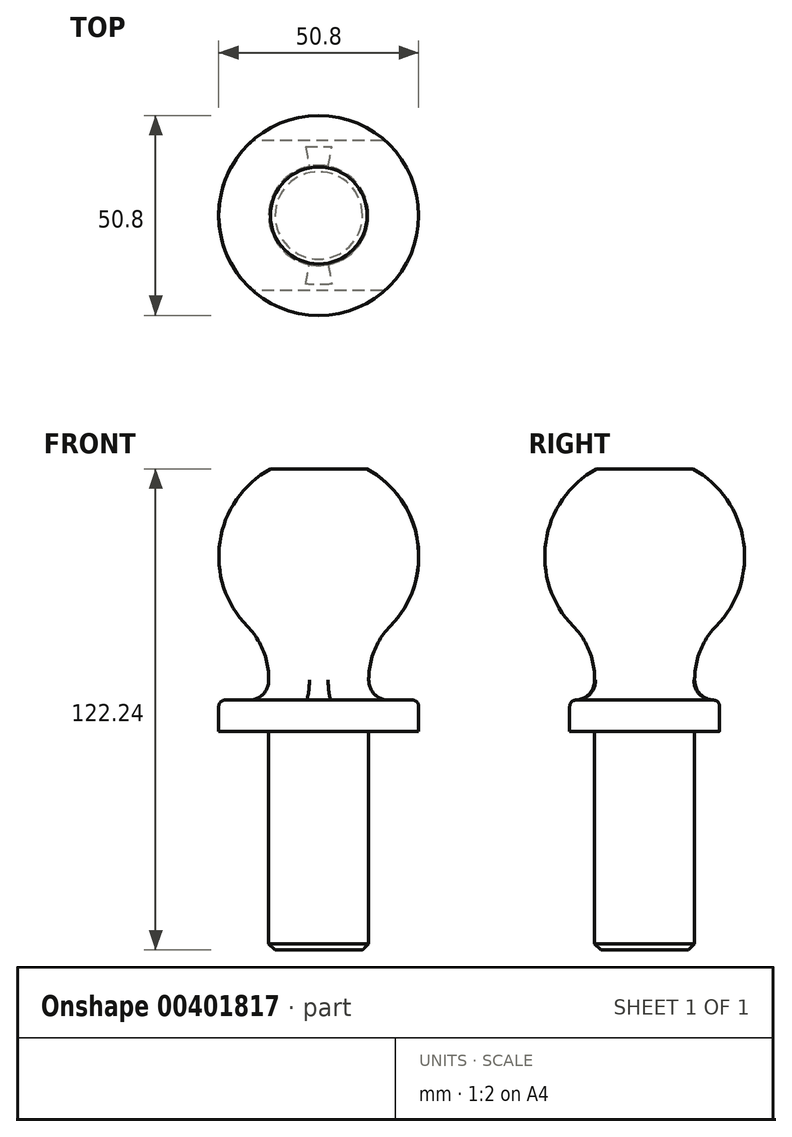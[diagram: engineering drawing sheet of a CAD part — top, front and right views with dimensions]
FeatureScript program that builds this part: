
annotation { "Feature Type Name" : "Feature", "Feature Type Description" : "" }
export const myFeature = defineFeature(function(context is Context, id is Id, definition is map)
    precondition{}
    {
        {
            var Q0;
            Q0=qCreatedBy(makeId("Front.planeOp"),FACE);
            var sketch = newSketch(context, id + "F0", { "sketchPlane" : qUnion([Q0])});
            skLineSegment(sketch, "E0.bottom", {"start": v(-12.7, 0) * mm, "end": v(-25.4, 0) * mm});
            skLineSegment(sketch, "E0.top", {"start": v(-12.7, 7.94) * mm, "end": v(-25.4, 7.94) * mm});
            skLineSegment(sketch, "E0.left", {"start": v(0, 0) * mm, "end": v(0, 7.94) * mm});
            skLineSegment(sketch, "E0.right", {"start": v(-25.4, 0) * mm, "end": v(-25.4, 7.94) * mm});
            skPoint(sketch, "E1", {"position": v(-12.7, 22.45) * mm});
            skPoint(sketch, "E2", {"position": v(0, 19.05) * mm});
            skLineSegment(sketch, "E3", {"start": v(-12.7, 22.45) * mm, "end": v(-12.7, 7.94) * mm});
            skPoint(sketch, "E4", {"position": v(-12.7, 7.94) * mm});
            skLineSegment(sketch, "E5", {"start": v(0, 66.68) * mm, "end": v(0, 19.05) * mm});
            skLineSegment(sketch, "E6", {"start": v(0, 19.05) * mm, "end": v(0, 7.94) * mm});
            skArc(sketch, "E7", {"start": v(-12.3, 66.68) * mm, "mid": v(-25.4, 44.68) * mm, "end": v(-12.7, 22.45) * mm});
            skLineSegment(sketch, "E8", {"start": v(0, 66.68) * mm, "end": v(-12.3, 66.68) * mm});
            skLineSegment(sketch, "E9.top", {"start": v(0, -55.56) * mm, "end": v(-12.7, -55.56) * mm});
            skLineSegment(sketch, "E9.left", {"start": v(0, 0) * mm, "end": v(0, -55.56) * mm});
            skLineSegment(sketch, "E9.right", {"start": v(-12.7, 0) * mm, "end": v(-12.7, -55.56) * mm});
            skSolve(sketch);
        }
        {
            var Q0;
            Q0 = qSketchRegion(id + "F0", true);
            var Q1;
            Q1=sQuery(id+"F0.wireOp",EDGE,"E9.left");
            revolve(context, id + "F1", {"entities" : qUnion([Q0]), "axis" : qUnion([Q1]), "revolveType" : RevolveType.FULL});
        }
        {
            var Q0;
            Q0=qCreatedBy(makeId("Right.planeOp"),FACE);
            var sketch = newSketch(context, id + "F2", { "sketchPlane" : qUnion([Q0])});
            skLineSegment(sketch, "E10.bottom", {"start": v(-49.59, -5.38) * mm, "end": v(-19.05, -5.38) * mm});
            skLineSegment(sketch, "E10.top", {"start": v(-49.59, 14.79) * mm, "end": v(-19.05, 14.79) * mm});
            skLineSegment(sketch, "E10.left", {"start": v(-49.59, -5.38) * mm, "end": v(-49.59, 14.79) * mm});
            skLineSegment(sketch, "E10.right", {"start": v(-19.05, -5.38) * mm, "end": v(-19.05, 14.79) * mm});
            skLineSegment(sketch, "E11.bottom", {"start": v(19.05, -5.38) * mm, "end": v(49.59, -5.38) * mm});
            skLineSegment(sketch, "E11.top", {"start": v(19.05, 14.79) * mm, "end": v(49.59, 14.79) * mm});
            skLineSegment(sketch, "E11.left", {"start": v(19.05, -5.38) * mm, "end": v(19.05, 14.79) * mm});
            skLineSegment(sketch, "E11.right", {"start": v(49.59, -5.38) * mm, "end": v(49.59, 14.79) * mm});
            skSolve(sketch);
        }
        {
            var Q0;
            Q0=makeQuery(id+"F2.imprint","IMPRINT",FACE,{"disambiguationData":[TD([[makeQuery(id+"F2.imprint","IMPRINT",EDGE,{"derivedFrom":sQuery(id+"F2.wireOp",EDGE,"E10.bottom")}),1.0]])]});
            var Q1;
            Q1=makeQuery(id+"F2.imprint","IMPRINT",FACE,{"disambiguationData":[TD([[makeQuery(id+"F2.imprint","IMPRINT",EDGE,{"derivedFrom":sQuery(id+"F2.wireOp",EDGE,"E11.bottom")}),1.0]])]});
            extrude(context, id + "F3", {"entities" : qUnion([Q0, Q1]), "operationType" : NewBodyOperationType.REMOVE, "endBound" : BoundingType.THROUGH_ALL, "oppositeDirection" : true, "depth" : 25.4 * mm, "hasSecondDirection" : true, "secondDirectionOppositeDirection" : false, "secondDirectionDepth" : 25.4 * mm});
        }
        {
            var Q0;
            Q0=makeQuery(id+"F3.boolean.opBoolean","SPLIT",EDGE,{"disambiguationData":[OD(1.0)],"derivedFrom":makeQuery(id+"F1.opRevolve","SWEPT_EDGE",EDGE,{"disambiguationData":[OSD([sQuery(id+"F0.wireOp",EDGE,"E0.top"),sQuery(id+"F0.wireOp",EDGE,"E0.right")])]})});
            var Q1;
            Q1=makeQuery(id+"F3.boolean.opBoolean","SPLIT",EDGE,{"disambiguationData":[OD(0.0)],"derivedFrom":makeQuery(id+"F1.opRevolve","SWEPT_EDGE",EDGE,{"disambiguationData":[OSD([sQuery(id+"F0.wireOp",EDGE,"E0.top"),sQuery(id+"F0.wireOp",EDGE,"E0.right")])]})});
            var Q2;
            Q2=makeQuery(id+"F3.boolean.opBoolean","INTERSECT",EDGE,{"derivedFrom":[makeQuery(id+"F1.opRevolve","SWEPT_FACE",FACE,{"disambiguationData":[OSD([sQuery(id+"F0.wireOp",EDGE,"E0.top")])]}),makeQuery(id+"F3.opExtrude","SWEPT_FACE",FACE,{"disambiguationData":[OSD([sQuery(id+"F2.wireOp",EDGE,"E10.right")])]})]});
            var Q3;
            Q3=makeQuery(id+"F3.boolean.opBoolean","INTERSECT",EDGE,{"derivedFrom":[makeQuery(id+"F1.opRevolve","SWEPT_FACE",FACE,{"disambiguationData":[OSD([sQuery(id+"F0.wireOp",EDGE,"E0.top")])]}),makeQuery(id+"F3.opExtrude","SWEPT_FACE",FACE,{"disambiguationData":[OSD([sQuery(id+"F2.wireOp",EDGE,"E11.left")])]})]});
            var Q4;
            Q4=makeQuery(id+"F3.boolean.opBoolean","INTERSECT",EDGE,{"disambiguationData":[OD(0.0)],"derivedFrom":[makeQuery(id+"F1.opRevolve","SWEPT_FACE",FACE,{"disambiguationData":[OSD([sQuery(id+"F0.wireOp",EDGE,"E0.right")])]}),makeQuery(id+"F3.opExtrude","SWEPT_FACE",FACE,{"disambiguationData":[OSD([sQuery(id+"F2.wireOp",EDGE,"E11.left")])]})]});
            var Q5;
            Q5=makeQuery(id+"F3.boolean.opBoolean","INTERSECT",EDGE,{"disambiguationData":[OD(1.0)],"derivedFrom":[makeQuery(id+"F1.opRevolve","SWEPT_FACE",FACE,{"disambiguationData":[OSD([sQuery(id+"F0.wireOp",EDGE,"E0.right")])]}),makeQuery(id+"F3.opExtrude","SWEPT_FACE",FACE,{"disambiguationData":[OSD([sQuery(id+"F2.wireOp",EDGE,"E11.left")])]})]});
            var Q6;
            Q6=makeQuery(id+"F3.boolean.opBoolean","INTERSECT",EDGE,{"disambiguationData":[OD(1.0)],"derivedFrom":[makeQuery(id+"F1.opRevolve","SWEPT_FACE",FACE,{"disambiguationData":[OSD([sQuery(id+"F0.wireOp",EDGE,"E0.right")])]}),makeQuery(id+"F3.opExtrude","SWEPT_FACE",FACE,{"disambiguationData":[OSD([sQuery(id+"F2.wireOp",EDGE,"E10.right")])]})]});
            var Q7;
            Q7=makeQuery(id+"F3.boolean.opBoolean","INTERSECT",EDGE,{"disambiguationData":[OD(0.0)],"derivedFrom":[makeQuery(id+"F1.opRevolve","SWEPT_FACE",FACE,{"disambiguationData":[OSD([sQuery(id+"F0.wireOp",EDGE,"E0.right")])]}),makeQuery(id+"F3.opExtrude","SWEPT_FACE",FACE,{"disambiguationData":[OSD([sQuery(id+"F2.wireOp",EDGE,"E10.right")])]})]});
            fillet(context, id + "F4", {"entities" : qUnion([Q0, Q1, Q2, Q3, Q4, Q5, Q6, Q7]), "radius" : 1.59 * mm, "tangentPropagation" : true, "allowEdgeOverflow" : false});
        }
        {
            var Q0;
            Q0=makeQuery(id+"F1.opRevolve","SWEPT_EDGE",EDGE,{"disambiguationData":[OSD([sQuery(id+"F0.wireOp",EDGE,"E9.top"),sQuery(id+"F0.wireOp",EDGE,"E9.right")])]});
            chamfer(context, id + "F5", {"entities" : qUnion([Q0]), "width" : 1.6 * mm, "tangentPropagation" : true});
        }
        {
            var Q0;
            Q0=makeQuery(id+"F1.opRevolve","SWEPT_EDGE",EDGE,{"disambiguationData":[OSD([sQuery(id+"F0.wireOp",EDGE,"E3"),sQuery(id+"F0.wireOp",EDGE,"E7")])]});
            fillet(context, id + "F6", {"entities" : qUnion([Q0]), "radius" : 19.05 * mm, "tangentPropagation" : true, "allowEdgeOverflow" : false});
        }
        {
            var Q0;
            Q0=makeQuery(id+"F1.opRevolve","SWEPT_EDGE",EDGE,{"disambiguationData":[OSD([sQuery(id+"F0.wireOp",EDGE,"E0.top"),sQuery(id+"F0.wireOp",EDGE,"E3")])]});
            fillet(context, id + "F7", {"entities" : qUnion([Q0]), "radius" : 5.08 * mm, "tangentPropagation" : true, "allowEdgeOverflow" : false});
        }
    });
